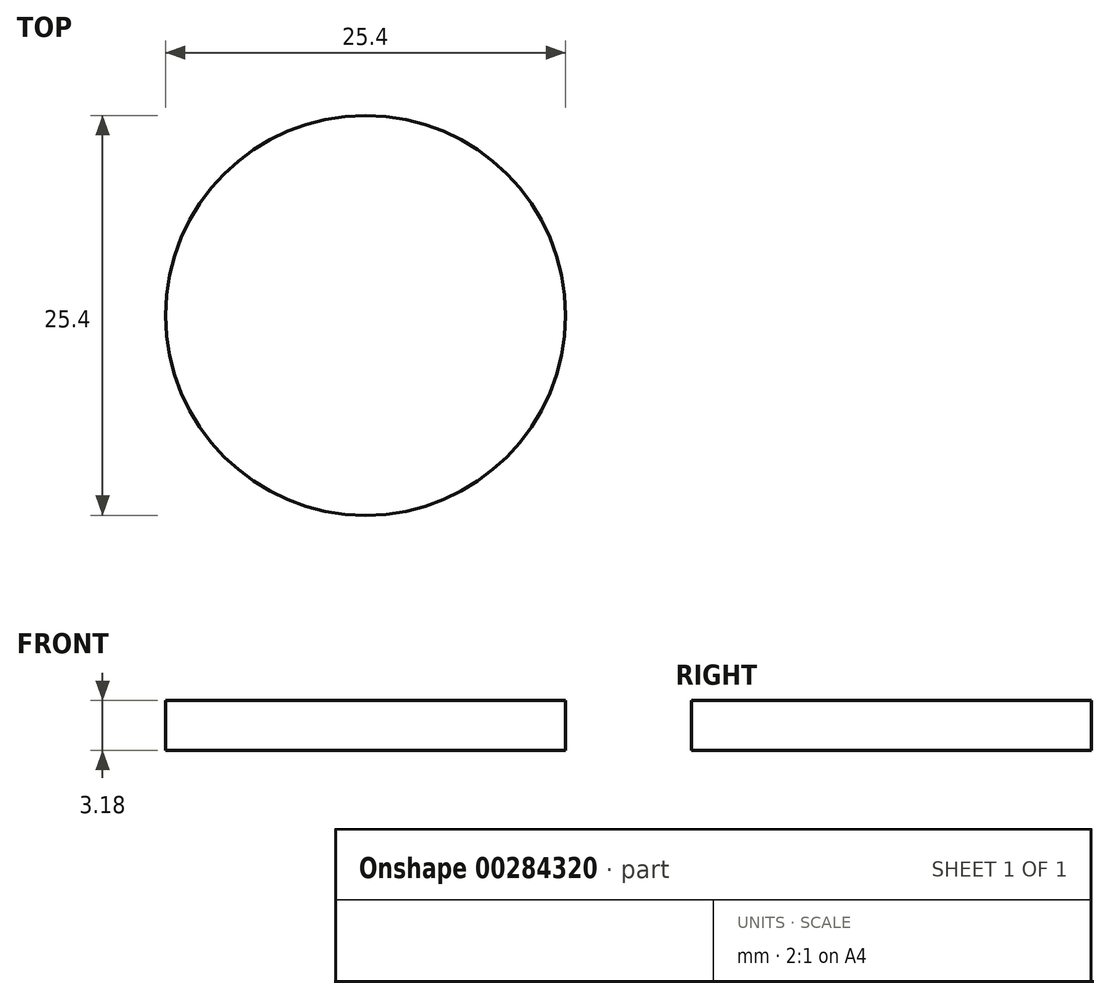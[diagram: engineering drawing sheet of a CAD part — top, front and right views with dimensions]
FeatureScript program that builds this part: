
annotation { "Feature Type Name" : "Feature", "Feature Type Description" : "" }
export const myFeature = defineFeature(function(context is Context, id is Id, definition is map)
    precondition{}
    {
        {
            var Q0;
            Q0=qCreatedBy(makeId("Top.planeOp"),FACE);
            var sketch = newSketch(context, id + "F0", { "sketchPlane" : qUnion([Q0])});
            skCircle(sketch, "E0", {"center": v(0, 0) * mm, "radius": 12.7 * mm});
            skSolve(sketch);
        }
        {
            var Q0;
            Q0=makeQuery(id+"F0.imprint","IMPRINT",FACE,{"disambiguationData":[TD([[makeQuery(id+"F0.imprint","IMPRINT",EDGE,{"derivedFrom":sQuery(id+"F0.wireOp",EDGE,"E0")}),1.0]])]});
            extrude(context, id + "F1", {"entities" : qUnion([Q0]), "depth" : 3.17 * mm});
        }
    });
